# Revit family: Hager-IC-Flush_mounted-IP40-With_Cover-With_DIN-NoHosted-PL-pl
name_source: partatom
category: Electrical Equipment
units: mm (PartAtom-declared; Revit-internal decimal feet)

## family parameters
Always vertical = Yes
Cut with Voids When Loaded = No
Maintain Annotation Orientation = No
Panel Configuration = Two Columns, Circuits Across
Part Type = Panelboard
Room Calculation Point = No
Round Connector Dimension = Use Diameter
Shared = No
Work Plane-Based = Yes

## types (2) — shared parameters
BC_METADATA = {"ObjectGuid":"bc35c96e-cb38-443e-833d-0616858cb9ac","ModelGuid":"8af03f69-2293-4735-a617-cc53adf55621","VariantGuid":"8b6e323b-1b53-409a-a940-11b5a7fc5337","Revision":"#4","VariantName":"Template-Enclosure_EU-EC000214"}
BC_MODEL_ID = 1554357
BC_OBJECT_ID = 513888
BC_OBJECT_VERSION = #5
Code hager = ADD-EC000214_EU
Default Elevation = 1200 mm
EF000003 - Sposób montażu = Montaż podtynkowy
EF000007 - Kolor = Biały
EF000008 - Szerokość = 308 mm  [stored 1.0105 ft]
EF000024 - Odporność na promieniowanie UV = No
EF000040 - Wysokość = 351 mm  [stored 1.15157 ft]
EF000049 - Głębokość = 93 mm  [stored 0.305118 ft]
EF000116 - Numer RAL = 9010
EF000118 - Z płytą montażową = No
EF000218 - Głębokość wbudowania = 72 mm  [stored 0.23622 ft]
EF000266 - Liczba rzędów = 2
EF000332 - Wysokość wbudowania = 333 mm  [stored 1.09252 ft]
EF000846 - Szerokość wbudowania = 290 mm  [stored 0.951444 ft]
EF001062 - Wykonanie zgodne z Dyrektywą Kompatybilności Elektromagnetycznej EMC = No
EF001088 - Możliwość rozbudowy = Yes
EF001134 - Szyna DIN = Yes
EF002950 - Szerokość wyrażona liczbą modułów = 12
EF004462 - Rodzaj zamknięcia = Inne
EF005474 - Stopień ochrony (IP) = IP40
EF006306 - Z zamkiem = No
EF009212 - Wykonanie/rodzaj pokrywy = Zamknięty
EF015776 - Listwa zaciskowa uziemienia = Yes
EF015777 - Listwa zaciskowa przewodu neutralnego = Yes
EF015941 - Drzwi przepuszczające sygnał = Yes
ETIM class code = EC000214
ETIM class name = Small distribution board
HG000001-Number of columns-pl = 1
HG000002-with door or cover-pl = Yes
HG000003-Range-pl = IC
HG000005-Thickness-pl = 2 mm  [stored 0.00656168 ft]
HG000006-Flush mounted-pl = Yes
HG000009-Double swing door-pl = No
HG000010-Asymmetric doors-pl = No
HG000011-Empty rows from bottom-pl = No
HG000012-Door swing angle-pl = 90.00°
HG000013-Door on the left-pl = No
HG000014-Door on the right-pl = Yes
HG000015-Clearance visibility-pl = Yes
HG000016-Door 3D visibility-pl = Yes
HG000017-Distance between poles-pl = 18 mm  [stored 0.0590551 ft]
HG000060-RAL-number = 9010
HG000099-Onfly Template ID-pl-PL = 507532
HGEF000266-Liczba rzędów = 2
HGEF0002950-Szerokość wyrażona liczbą modułów = 12
Manufacturer = Hager
Name = IC-Flush_mounted-IP40-With_Cover-With_DIN-PL
Name BIM&CO = Electricity
Name hager = ADD_Enclosures_EC000214
Uniformat = Low Tension Service & Dist.
Uniformat code = D501001
zero-valued in all types: EF001131 - Głębokość wewnętrzna, HG000007-Number of empty columns-pl, HG000008-Number of empty rows-pl

## per-type parameters (varying)
| type | BC_VARIANT_ID | EF006244 - Transparentna pokrywa/drzwi | HG000004-Manufacturer reference-pl |
| IC-Flush_mounted_W308_H351_D93_12_Modular_Spacing-VR212PP | 1178993 | No | VR212PP |
| IC-Flush_mounted_W308_H351_D93_12_Modular_Spacing-VR212TP | 1178994 | Yes | VR212TP |

note: column(s) folded — value = type name in every type: Reference

note: [stored X ft] marks values corroborated as IEEE doubles in the binary element streams (Revit-internal decimal feet)

## geometry (parser evidence)
native form markers: Sweep x14
no freeform markers — native parametric forms only
